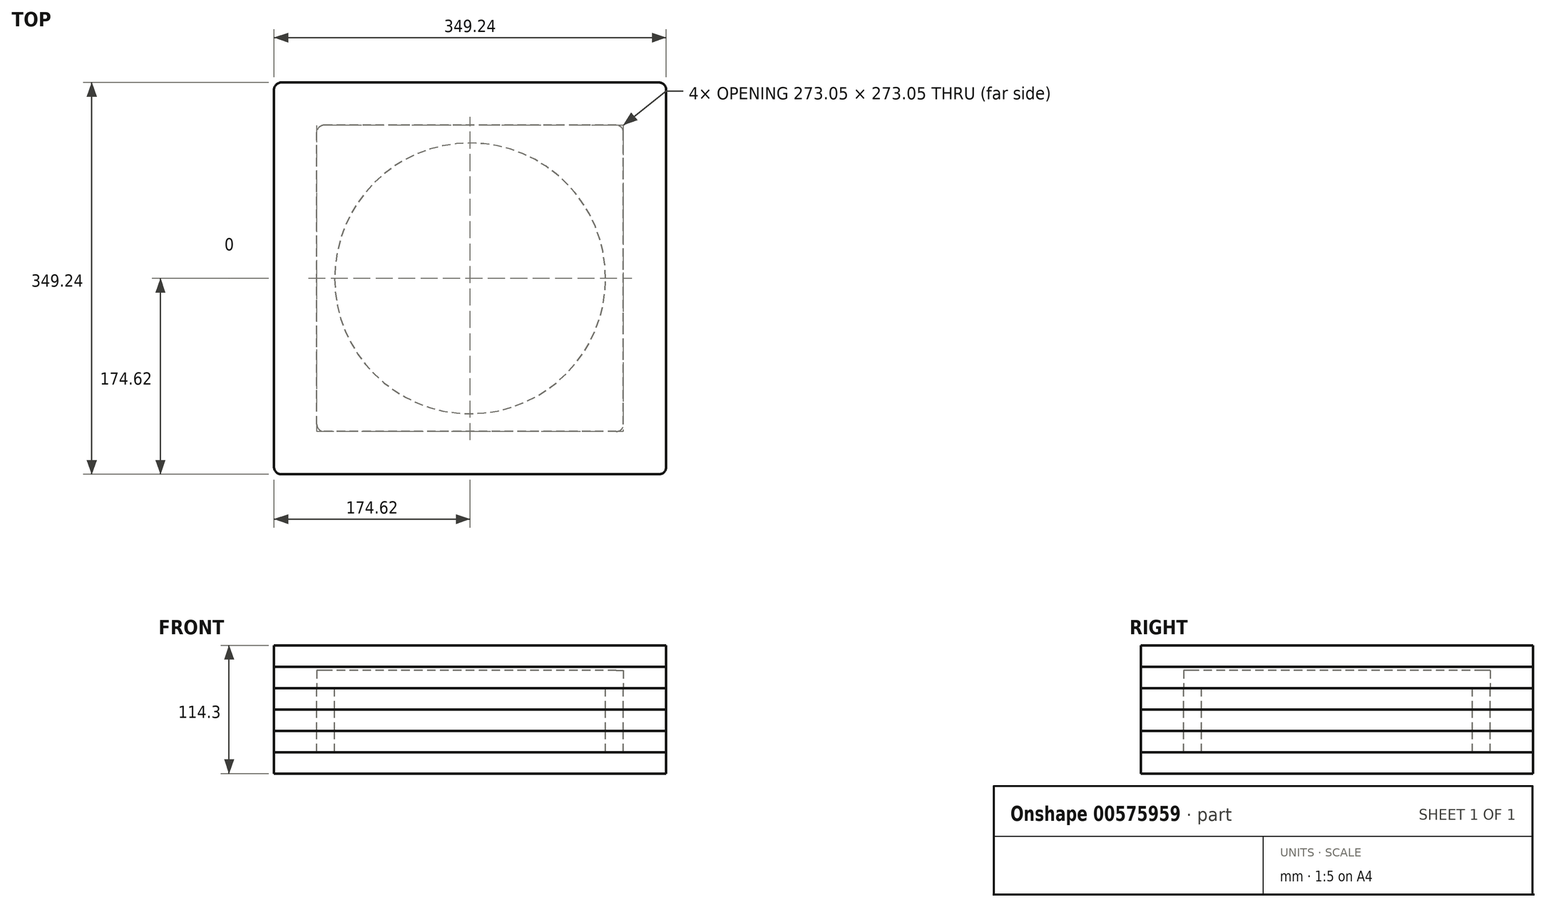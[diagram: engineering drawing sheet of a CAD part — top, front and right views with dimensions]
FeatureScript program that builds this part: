
annotation { "Feature Type Name" : "Feature", "Feature Type Description" : "" }
export const myFeature = defineFeature(function(context is Context, id is Id, definition is map)
    precondition{}
    {
        {
            var Q0;
            Q0=qCreatedBy(makeId("Top.planeOp"),FACE);
            var sketch = newSketch(context, id + "F0", { "sketchPlane" : qUnion([Q0])});
            skLineSegment(sketch, "E0.bottom", {"start": v(174.63, -174.63) * mm, "end": v(-174.62, -174.63) * mm});
            skLineSegment(sketch, "E0.top", {"start": v(174.62, 174.63) * mm, "end": v(-174.63, 174.62) * mm});
            skLineSegment(sketch, "E0.left", {"start": v(174.63, -174.63) * mm, "end": v(174.62, 174.63) * mm});
            skLineSegment(sketch, "E0.right", {"start": v(-174.62, -174.63) * mm, "end": v(-174.63, 174.62) * mm});
            skPoint(sketch, "E0.middle", {"position": v(0, 0) * mm});
            skSolve(sketch);
        }
        {
            var Q0;
            Q0=makeQuery(id+"F0.imprint","IMPRINT",FACE,{"disambiguationData":[TD([[makeQuery(id+"F0.imprint","IMPRINT",EDGE,{"derivedFrom":sQuery(id+"F0.wireOp",EDGE,"E0.bottom")}),-1.0]])]});
            extrude(context, id + "F1", {"entities" : qUnion([Q0]), "depth" : 19.05 * mm, "offsetDistance" : 25.4 * mm});
        }
        {
            var Q0;
            Q0=makeQuery(id+"F1.opExtrude","SWEPT_EDGE",EDGE,{"disambiguationData":[OSD([sQuery(id+"F0.wireOp",EDGE,"E0.bottom"),sQuery(id+"F0.wireOp",EDGE,"E0.left")])]});
            var Q1;
            Q1=makeQuery(id+"F1.opExtrude","SWEPT_EDGE",EDGE,{"disambiguationData":[OSD([sQuery(id+"F0.wireOp",EDGE,"E0.top"),sQuery(id+"F0.wireOp",EDGE,"E0.left")])]});
            var Q2;
            Q2=makeQuery(id+"F1.opExtrude","SWEPT_EDGE",EDGE,{"disambiguationData":[OSD([sQuery(id+"F0.wireOp",EDGE,"E0.top"),sQuery(id+"F0.wireOp",EDGE,"E0.right")])]});
            var Q3;
            Q3=makeQuery(id+"F1.opExtrude","SWEPT_EDGE",EDGE,{"disambiguationData":[OSD([sQuery(id+"F0.wireOp",EDGE,"E0.bottom"),sQuery(id+"F0.wireOp",EDGE,"E0.right")])]});
            fillet(context, id + "F2", {"entities" : qUnion([Q0, Q1, Q2, Q3]), "radius" : 6.35 * mm, "tangentPropagation" : true, "allowEdgeOverflow" : false});
        }
        {
            var Q0;
            Q0=makeQuery(id+"F1.opExtrude","SWEPT_BODY",BODY,{"disambiguationData":[OSD([sQuery(id+"F0.wireOp",EDGE,"E0.bottom"),sQuery(id+"F0.wireOp",EDGE,"E0.top"),sQuery(id+"F0.wireOp",EDGE,"E0.left"),sQuery(id+"F0.wireOp",EDGE,"E0.right")])]});
            transform(context, id + "F3", {"entities" : qUnion([Q0]), "transformType" : TransformType.TRANSLATION_3D, "dx" : 0 * mm, "dy" : 0 * mm, "dz" : 19.05 * mm, "makeCopy" : true});
        }
        {
            var Q0;
            Q0=makeQuery(id+"F3.opPattern","COPY",FACE,{"derivedFrom":makeQuery(id+"F1.opExtrude","CAP_FACE",FACE,{"disambiguationData":[OSD([sQuery(id+"F0.wireOp",EDGE,"E0.bottom"),sQuery(id+"F0.wireOp",EDGE,"E0.top"),sQuery(id+"F0.wireOp",EDGE,"E0.left"),sQuery(id+"F0.wireOp",EDGE,"E0.right")])],"isStart":false}),"instanceName":"1"});
            var sketch = newSketch(context, id + "F4", { "sketchPlane" : qUnion([Q0])});
            skCircle(sketch, "E1", {"center": v(0, 0) * mm, "radius": 120.65 * mm});
            skLineSegment(sketch, "E2.bottom", {"start": v(136.53, -136.52) * mm, "end": v(-136.52, -136.53) * mm});
            skLineSegment(sketch, "E2.top", {"start": v(136.53, 136.53) * mm, "end": v(-136.53, 136.52) * mm});
            skLineSegment(sketch, "E2.left", {"start": v(136.53, -136.52) * mm, "end": v(136.52, 136.53) * mm});
            skLineSegment(sketch, "E2.right", {"start": v(-136.53, -136.53) * mm, "end": v(-136.53, 136.53) * mm});
            skSolve(sketch);
        }
        {
            var Q0;
            Q0=makeQuery(id+"F4.imprint","IMPRINT",FACE,{"disambiguationData":[TD([[makeQuery(id+"F4.imprint","IMPRINT",EDGE,{"derivedFrom":sQuery(id+"F4.wireOp",EDGE,"E1")}),-1.0]])]});
            extrude(context, id + "F5", {"entities" : qUnion([Q0]), "operationType" : NewBodyOperationType.REMOVE, "oppositeDirection" : true, "depth" : 19.05 * mm, "offsetDistance" : 25.4 * mm});
        }
        {
            var Q0;
            Q0=makeQuery(id+"F5.boolean.opBoolean","COPY",EDGE,{"derivedFrom":makeQuery(id+"F5.opExtrude","SWEPT_EDGE",EDGE,{"disambiguationData":[OSD([sQuery(id+"F4.wireOp",EDGE,"E2.bottom"),sQuery(id+"F4.wireOp",EDGE,"E2.right")])]})});
            var Q1;
            Q1=makeQuery(id+"F5.boolean.opBoolean","COPY",EDGE,{"derivedFrom":makeQuery(id+"F5.opExtrude","SWEPT_EDGE",EDGE,{"disambiguationData":[OSD([sQuery(id+"F4.wireOp",EDGE,"E2.top"),sQuery(id+"F4.wireOp",EDGE,"E2.left")])]})});
            var Q2;
            Q2=makeQuery(id+"F5.boolean.opBoolean","COPY",EDGE,{"derivedFrom":makeQuery(id+"F5.opExtrude","SWEPT_EDGE",EDGE,{"disambiguationData":[OSD([sQuery(id+"F4.wireOp",EDGE,"E2.top"),sQuery(id+"F4.wireOp",EDGE,"E2.right")])]})});
            var Q3;
            Q3=makeQuery(id+"F5.boolean.opBoolean","COPY",EDGE,{"derivedFrom":makeQuery(id+"F5.opExtrude","SWEPT_EDGE",EDGE,{"disambiguationData":[OSD([sQuery(id+"F4.wireOp",EDGE,"E2.bottom"),sQuery(id+"F4.wireOp",EDGE,"E2.left")])]})});
            fillet(context, id + "F6", {"entities" : qUnion([Q0, Q1, Q2, Q3]), "radius" : 6.35 * mm, "tangentPropagation" : true, "allowEdgeOverflow" : false});
        }
        {
            var Q0;
            Q0=makeQuery(id+"F5.boolean.opBoolean","SPLIT",BODY,{"disambiguationData":[OD(0.0)],"derivedFrom":makeQuery(id+"F3.opPattern","COPY",BODY,{"derivedFrom":makeQuery(id+"F1.opExtrude","SWEPT_BODY",BODY,{"disambiguationData":[OSD([sQuery(id+"F0.wireOp",EDGE,"E0.bottom"),sQuery(id+"F0.wireOp",EDGE,"E0.top"),sQuery(id+"F0.wireOp",EDGE,"E0.left"),sQuery(id+"F0.wireOp",EDGE,"E0.right")])]}),"instanceName":"1"})});
            transform(context, id + "F7", {"entities" : qUnion([Q0]), "transformType" : TransformType.TRANSLATION_3D, "dx" : 0 * mm, "dy" : 0 * mm, "dz" : 19.05 * mm, "makeCopy" : true});
        }
        {
            var Q0;
            Q0=makeQuery(id+"F5.boolean.opBoolean","SPLIT",BODY,{"disambiguationData":[OD(1.0)],"derivedFrom":makeQuery(id+"F3.opPattern","COPY",BODY,{"derivedFrom":makeQuery(id+"F1.opExtrude","SWEPT_BODY",BODY,{"disambiguationData":[OSD([sQuery(id+"F0.wireOp",EDGE,"E0.bottom"),sQuery(id+"F0.wireOp",EDGE,"E0.top"),sQuery(id+"F0.wireOp",EDGE,"E0.left"),sQuery(id+"F0.wireOp",EDGE,"E0.right")])]}),"instanceName":"1"})});
            transform(context, id + "F8", {"entities" : qUnion([Q0]), "transformType" : TransformType.TRANSLATION_3D, "dx" : 0 * mm, "dy" : 0 * mm, "dz" : 19.05 * mm, "makeCopy" : true});
        }
        {
            var Q0;
            Q0=makeQuery(id+"F7.opPattern","COPY",BODY,{"derivedFrom":makeQuery(id+"F5.boolean.opBoolean","SPLIT",BODY,{"disambiguationData":[OD(0.0)],"derivedFrom":makeQuery(id+"F3.opPattern","COPY",BODY,{"derivedFrom":makeQuery(id+"F1.opExtrude","SWEPT_BODY",BODY,{"disambiguationData":[OSD([sQuery(id+"F0.wireOp",EDGE,"E0.bottom"),sQuery(id+"F0.wireOp",EDGE,"E0.top"),sQuery(id+"F0.wireOp",EDGE,"E0.left"),sQuery(id+"F0.wireOp",EDGE,"E0.right")])]}),"instanceName":"1"})}),"instanceName":"1"});
            transform(context, id + "F9", {"entities" : qUnion([Q0]), "transformType" : TransformType.TRANSLATION_3D, "dx" : 0 * mm, "dy" : 0 * mm, "dz" : 19.05 * mm, "makeCopy" : true});
        }
        {
            var Q0;
            Q0=makeQuery(id+"F1.opExtrude","SWEPT_BODY",BODY,{"disambiguationData":[OSD([sQuery(id+"F0.wireOp",EDGE,"E0.bottom"),sQuery(id+"F0.wireOp",EDGE,"E0.top"),sQuery(id+"F0.wireOp",EDGE,"E0.left"),sQuery(id+"F0.wireOp",EDGE,"E0.right")])]});
            transform(context, id + "F10", {"entities" : qUnion([Q0]), "transformType" : TransformType.TRANSLATION_3D, "dx" : 0 * mm, "dy" : 0 * mm, "dz" : 76.2 * mm, "makeCopy" : true});
        }
        {
            var Q0;
            Q0=makeQuery(id+"F10.opPattern","COPY",FACE,{"derivedFrom":makeQuery(id+"F1.opExtrude","CAP_FACE",FACE,{"disambiguationData":[OSD([sQuery(id+"F0.wireOp",EDGE,"E0.bottom"),sQuery(id+"F0.wireOp",EDGE,"E0.top"),sQuery(id+"F0.wireOp",EDGE,"E0.left"),sQuery(id+"F0.wireOp",EDGE,"E0.right")])],"isStart":true}),"instanceName":"1"});
            var sketch = newSketch(context, id + "F11", { "sketchPlane" : qUnion([Q0])});
            skLineSegment(sketch, "E3.bottom", {"start": v(136.53, -136.52) * mm, "end": v(-136.52, -136.53) * mm});
            skLineSegment(sketch, "E3.top", {"start": v(136.52, 136.53) * mm, "end": v(-136.53, 136.52) * mm});
            skLineSegment(sketch, "E3.left", {"start": v(136.53, -136.52) * mm, "end": v(136.52, 136.53) * mm});
            skLineSegment(sketch, "E3.right", {"start": v(-136.52, -136.53) * mm, "end": v(-136.53, 136.52) * mm});
            skPoint(sketch, "E3.middle", {"position": v(0, 0) * mm});
            skSolve(sketch);
        }
        {
            var Q0;
            Q0 = qSketchRegion(id + "F11", true);
            extrude(context, id + "F12", {"entities" : qUnion([Q0]), "operationType" : NewBodyOperationType.REMOVE, "oppositeDirection" : true, "depth" : 15.88 * mm, "offsetDistance" : 25.4 * mm});
        }
        {
            var Q0;
            Q0=makeQuery(id+"F12.boolean.opBoolean","COPY",EDGE,{"derivedFrom":makeQuery(id+"F12.opExtrude","SWEPT_EDGE",EDGE,{"disambiguationData":[OSD([sQuery(id+"F11.wireOp",EDGE,"E3.top"),sQuery(id+"F11.wireOp",EDGE,"E3.right")])]})});
            var Q1;
            Q1=makeQuery(id+"F12.boolean.opBoolean","COPY",EDGE,{"derivedFrom":makeQuery(id+"F12.opExtrude","SWEPT_EDGE",EDGE,{"disambiguationData":[OSD([sQuery(id+"F11.wireOp",EDGE,"E3.bottom"),sQuery(id+"F11.wireOp",EDGE,"E3.right")])]})});
            var Q2;
            Q2=makeQuery(id+"F12.boolean.opBoolean","COPY",EDGE,{"derivedFrom":makeQuery(id+"F12.opExtrude","SWEPT_EDGE",EDGE,{"disambiguationData":[OSD([sQuery(id+"F11.wireOp",EDGE,"E3.top"),sQuery(id+"F11.wireOp",EDGE,"E3.left")])]})});
            var Q3;
            Q3=makeQuery(id+"F12.boolean.opBoolean","COPY",EDGE,{"derivedFrom":makeQuery(id+"F12.opExtrude","SWEPT_EDGE",EDGE,{"disambiguationData":[OSD([sQuery(id+"F11.wireOp",EDGE,"E3.bottom"),sQuery(id+"F11.wireOp",EDGE,"E3.left")])]})});
            fillet(context, id + "F13", {"entities" : qUnion([Q0, Q1, Q2, Q3]), "radius" : 6.35 * mm, "tangentPropagation" : true, "allowEdgeOverflow" : false});
        }
        {
            var Q0;
            Q0=makeQuery(id+"F1.opExtrude","SWEPT_BODY",BODY,{"disambiguationData":[OSD([sQuery(id+"F0.wireOp",EDGE,"E0.bottom"),sQuery(id+"F0.wireOp",EDGE,"E0.top"),sQuery(id+"F0.wireOp",EDGE,"E0.left"),sQuery(id+"F0.wireOp",EDGE,"E0.right")])]});
            transform(context, id + "F14", {"entities" : qUnion([Q0]), "transformType" : TransformType.TRANSLATION_3D, "dx" : 0 * mm, "dy" : 0 * mm, "dz" : 95.25 * mm, "makeCopy" : true});
        }
    });
